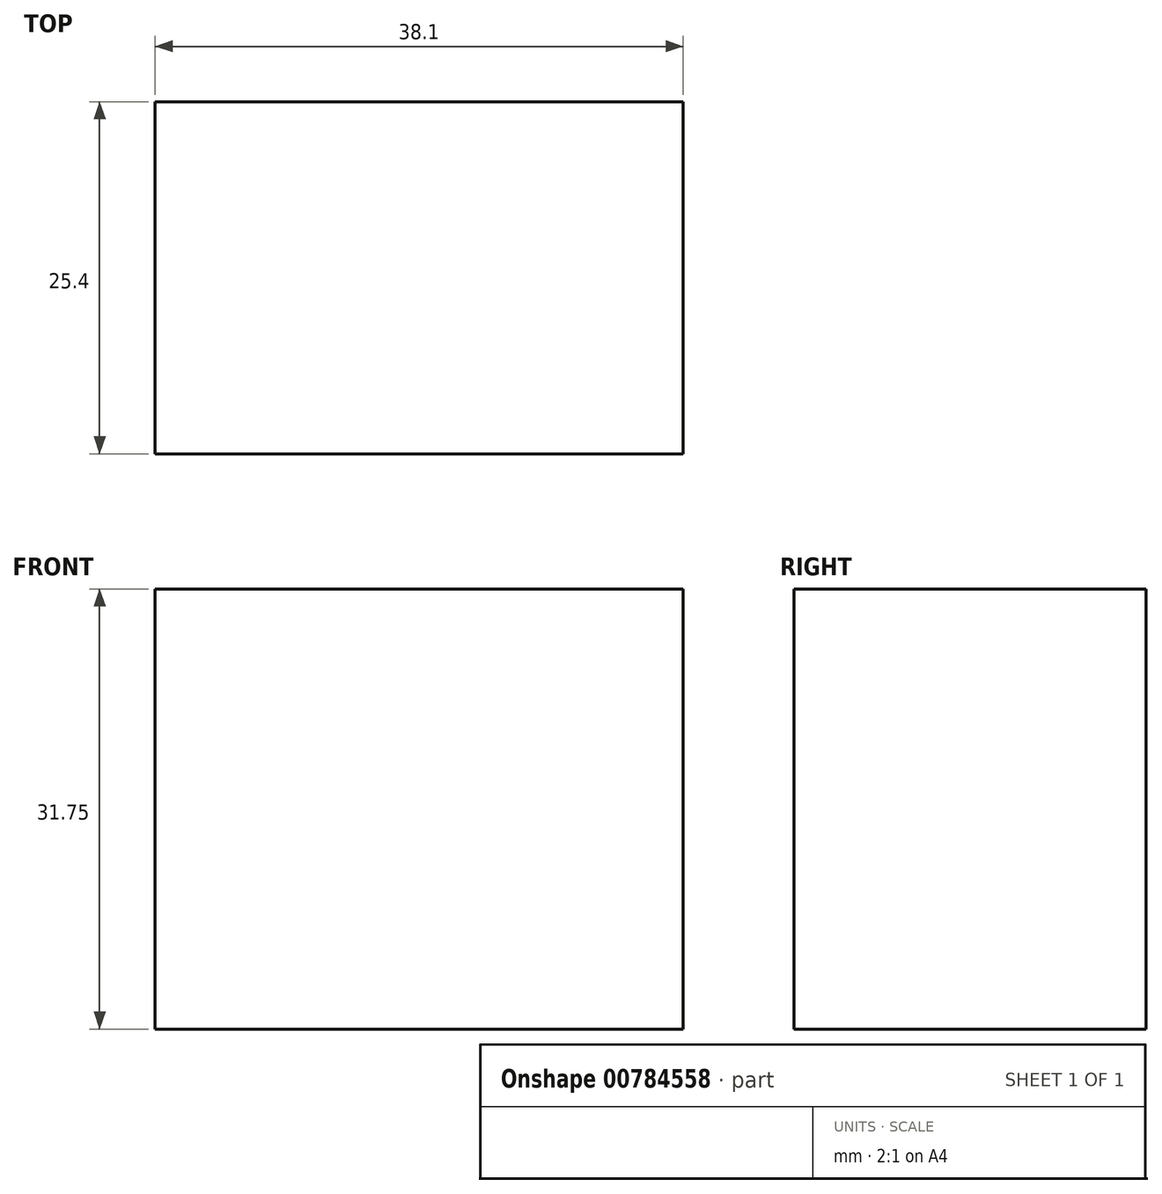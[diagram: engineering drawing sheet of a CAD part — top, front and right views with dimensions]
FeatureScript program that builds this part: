
annotation { "Feature Type Name" : "Feature", "Feature Type Description" : "" }
export const myFeature = defineFeature(function(context is Context, id is Id, definition is map)
    precondition{}
    {
        {
            var Q0;
            Q0=qCreatedBy(makeId("Front.planeOp"),FACE);
            var sketch = newSketch(context, id + "F0", { "sketchPlane" : qUnion([Q0])});
            skLineSegment(sketch, "E0", {"start": v(0, 0) * mm, "end": v(0, 31.75) * mm});
            skLineSegment(sketch, "E1", {"start": v(0, 0) * mm, "end": v(38.1, 0) * mm});
            skLineSegment(sketch, "E2", {"start": v(38.1, 0) * mm, "end": v(38.1, 31.75) * mm});
            skLineSegment(sketch, "E3", {"start": v(38.1, 31.75) * mm, "end": v(0, 31.75) * mm});
            skSolve(sketch);
        }
        {
            var Q0;
            Q0=makeQuery(id+"F0.imprint","IMPRINT",FACE,{"disambiguationData":[TD([[makeQuery(id+"F0.imprint","IMPRINT",EDGE,{"derivedFrom":sQuery(id+"F0.wireOp",EDGE,"E0")}),-1.0]])]});
            extrude(context, id + "F1", {"entities" : qUnion([Q0]), "depth" : 25.4 * mm, "offsetDistance" : 25.4 * mm});
        }
    });
